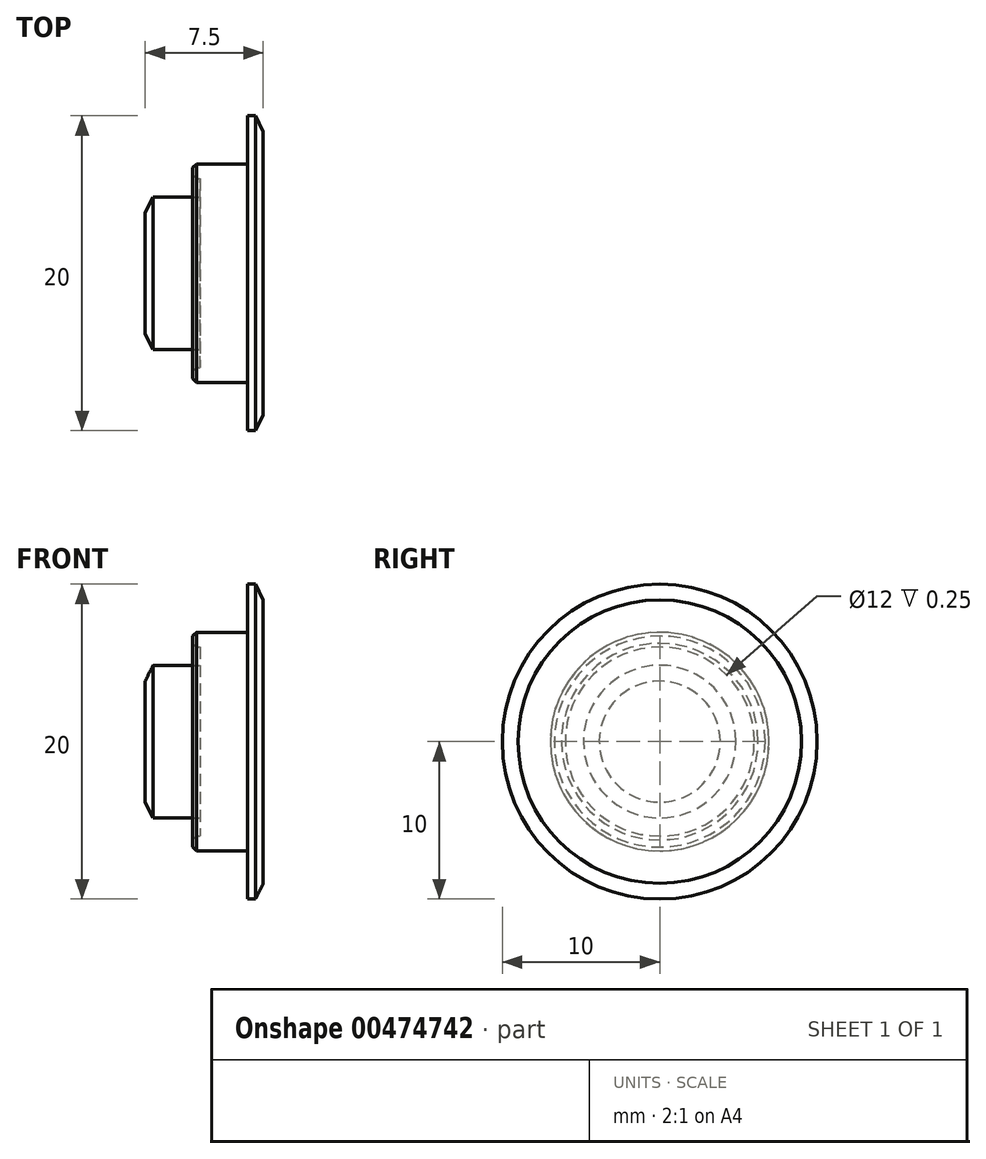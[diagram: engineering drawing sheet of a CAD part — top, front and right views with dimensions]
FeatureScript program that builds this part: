
annotation { "Feature Type Name" : "Feature", "Feature Type Description" : "" }
export const myFeature = defineFeature(function(context is Context, id is Id, definition is map)
    precondition{}
    {
        {
            var Q0;
            Q0=qCreatedBy(makeId("Right.planeOp"),FACE);
            var sketch = newSketch(context, id + "F0", { "sketchPlane" : qUnion([Q0])});
            skCircle(sketch, "E0", {"center": v(0, 0) * mm, "radius": 10 * mm});
            skSolve(sketch);
        }
        {
            var Q0;
            Q0 = qSketchRegion(id + "F0", true);
            extrude(context, id + "F1", {"entities" : qUnion([Q0]), "depth" : 4 * mm, "offsetDistance" : 25 * mm});
        }
        {
            var Q0;
            Q0=makeQuery(id+"F1.opExtrude","CAP_FACE",FACE,{"disambiguationData":[OSD([sQuery(id+"F0.wireOp",EDGE,"E0")])],"isStart":true});
            var sketch = newSketch(context, id + "F2", { "sketchPlane" : qUnion([Q0])});
            skCircle(sketch, "E1", {"center": v(0, 0) * mm, "radius": 4.85 * mm});
            skSolve(sketch);
        }
        {
            var Q0;
            Q0 = qSketchRegion(id + "F2", true);
            extrude(context, id + "F3", {"entities" : qUnion([Q0]), "operationType" : NewBodyOperationType.ADD, "depth" : 3.5 * mm, "offsetDistance" : 25 * mm});
        }
        {
            var Q0;
            Q0=makeQuery(id+"F1.opExtrude","CAP_FACE",FACE,{"disambiguationData":[OSD([sQuery(id+"F0.wireOp",EDGE,"E0")])],"isStart":true});
            var sketch = newSketch(context, id + "F4", { "sketchPlane" : qUnion([Q0])});
            skCircle(sketch, "E2", {"center": v(0, 0) * mm, "radius": 6.95 * mm});
            skCircle(sketch, "E3", {"center": v(0, 0) * mm, "radius": 6 * mm});
            skSolve(sketch);
        }
        {
            var Q0;
            Q0 = qSketchRegion(id + "F4", true);
            extrude(context, id + "F5", {"entities" : qUnion([Q0]), "operationType" : NewBodyOperationType.ADD, "depth" : 0.5 * mm, "offsetDistance" : 25 * mm});
        }
        {
            var Q0;
            {var subQ0=sQuery(id+"F0.wireOp",EDGE,"E0");Q0=makeQuery(id+"F5.boolean.opBoolean","SPLIT",FACE,{"disambiguationData":[TD([makeQuery(id+"F1.opExtrude","SWEPT_FACE",FACE,{"disambiguationData":[OSD([subQ0])]})])],"derivedFrom":makeQuery(id+"F1.opExtrude","CAP_FACE",FACE,{"disambiguationData":[OSD([subQ0])],"isStart":true})});}
            var sketch = newSketch(context, id + "F6", { "sketchPlane" : qUnion([Q0])});
            skCircle(sketch, "E4", {"center": v(0, 0) * mm, "radius": 10 * mm});
            skCircle(sketch, "E5", {"center": v(0, 0) * mm, "radius": 6.95 * mm});
            skSolve(sketch);
        }
        {
            var Q0;
            Q0 = qSketchRegion(id + "F6", true);
            extrude(context, id + "F7", {"entities" : qUnion([Q0]), "operationType" : NewBodyOperationType.REMOVE, "oppositeDirection" : true, "depth" : 3 * mm, "offsetDistance" : 25 * mm});
        }
        {
            var Q0;
            Q0=makeQuery(id+"F5.opExtrude","CAP_EDGE",EDGE,{"disambiguationData":[OSD([sQuery(id+"F4.wireOp",EDGE,"E2")])],"isStart":false});
            var Q1;
            Q1=makeQuery(id+"F5.opExtrude","CAP_EDGE",EDGE,{"disambiguationData":[OSD([sQuery(id+"F4.wireOp",EDGE,"E3")])],"isStart":false});
            chamfer(context, id + "F8", {"entities" : qUnion([Q0, Q1]), "width" : 0.25 * mm, "tangentPropagation" : true});
        }
        {
            var Q0;
            Q0=makeQuery(id+"F1.opExtrude","CAP_EDGE",EDGE,{"disambiguationData":[OSD([sQuery(id+"F0.wireOp",EDGE,"E0")])],"isStart":false});
            var Q1;
            Q1=makeQuery(id+"F3.opExtrude","CAP_EDGE",EDGE,{"disambiguationData":[OSD([sQuery(id+"F2.wireOp",EDGE,"E1")])],"isStart":false});
            chamfer(context, id + "F9", {"entities" : qUnion([Q0, Q1]), "chamferType" : ChamferType.TWO_OFFSETS, "width1" : 0.5 * mm, "oppositeDirection" : false, "width2" : 1 * mm, "tangentPropagation" : true});
        }
    });
